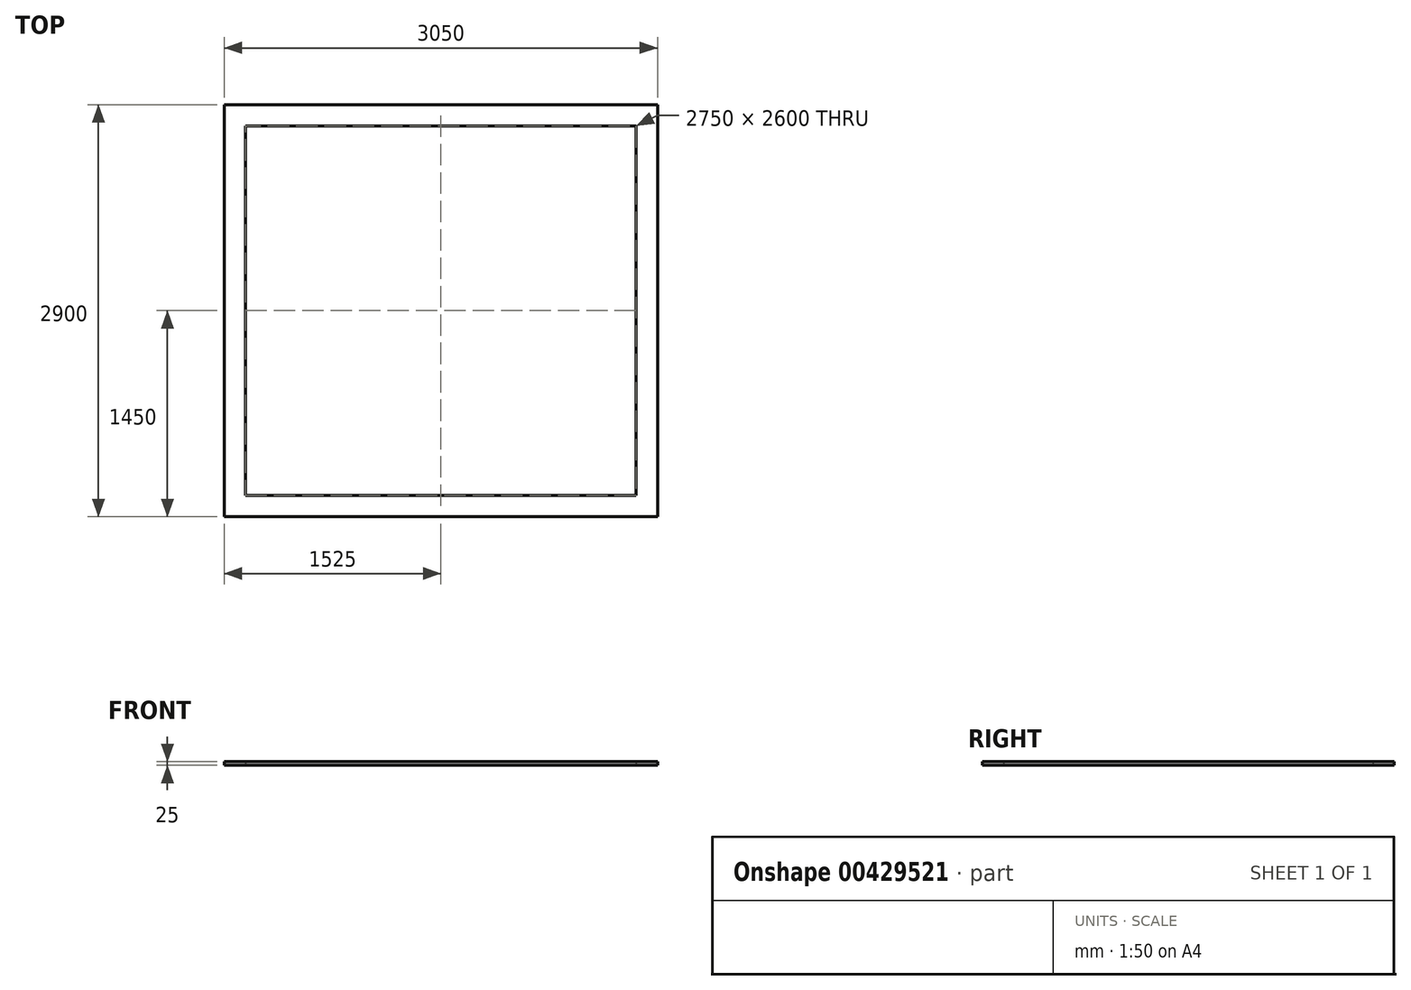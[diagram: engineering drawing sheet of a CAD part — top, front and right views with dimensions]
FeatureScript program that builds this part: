
annotation { "Feature Type Name" : "Feature", "Feature Type Description" : "" }
export const myFeature = defineFeature(function(context is Context, id is Id, definition is map)
    precondition{}
    {
        {
            var Q0;
            Q0=qCreatedBy(makeId("Top.planeOp"),FACE);
            var sketch = newSketch(context, id + "F0", { "sketchPlane" : qUnion([Q0])});
            skLineSegment(sketch, "E0.bottom", {"start": v(1375, 1300) * mm, "end": v(-1375, 1300) * mm});
            skLineSegment(sketch, "E0.top", {"start": v(1375, -1300) * mm, "end": v(-1375, -1300) * mm});
            skLineSegment(sketch, "E0.left", {"start": v(1375, 1300) * mm, "end": v(1375, -1300) * mm});
            skLineSegment(sketch, "E0.right", {"start": v(-1375, 1300) * mm, "end": v(-1375, -1300) * mm});
            skPoint(sketch, "E0.middle", {"position": v(0, 0) * mm});
            skLineSegment(sketch, "E1.0", {"start": v(-1525, 1450) * mm, "end": v(-1525, -1450) * mm});
            skLineSegment(sketch, "E1.1", {"start": v(1525, 1450) * mm, "end": v(-1525, 1450) * mm});
            skLineSegment(sketch, "E1.2", {"start": v(1525, 1450) * mm, "end": v(1525, -1450) * mm});
            skLineSegment(sketch, "E1.3", {"start": v(1525, -1450) * mm, "end": v(-1525, -1450) * mm});
            skSolve(sketch);
        }
        {
            var Q0;
            Q0=makeQuery(id+"F0.imprint","IMPRINT",FACE,{"disambiguationData":[TD([[makeQuery(id+"F0.imprint","IMPRINT",EDGE,{"derivedFrom":sQuery(id+"F0.wireOp",EDGE,"E0.bottom")}),-1.0]])]});
            extrude(context, id + "F1", {"entities" : qUnion([Q0]), "depth" : 25 * mm});
        }
    });
